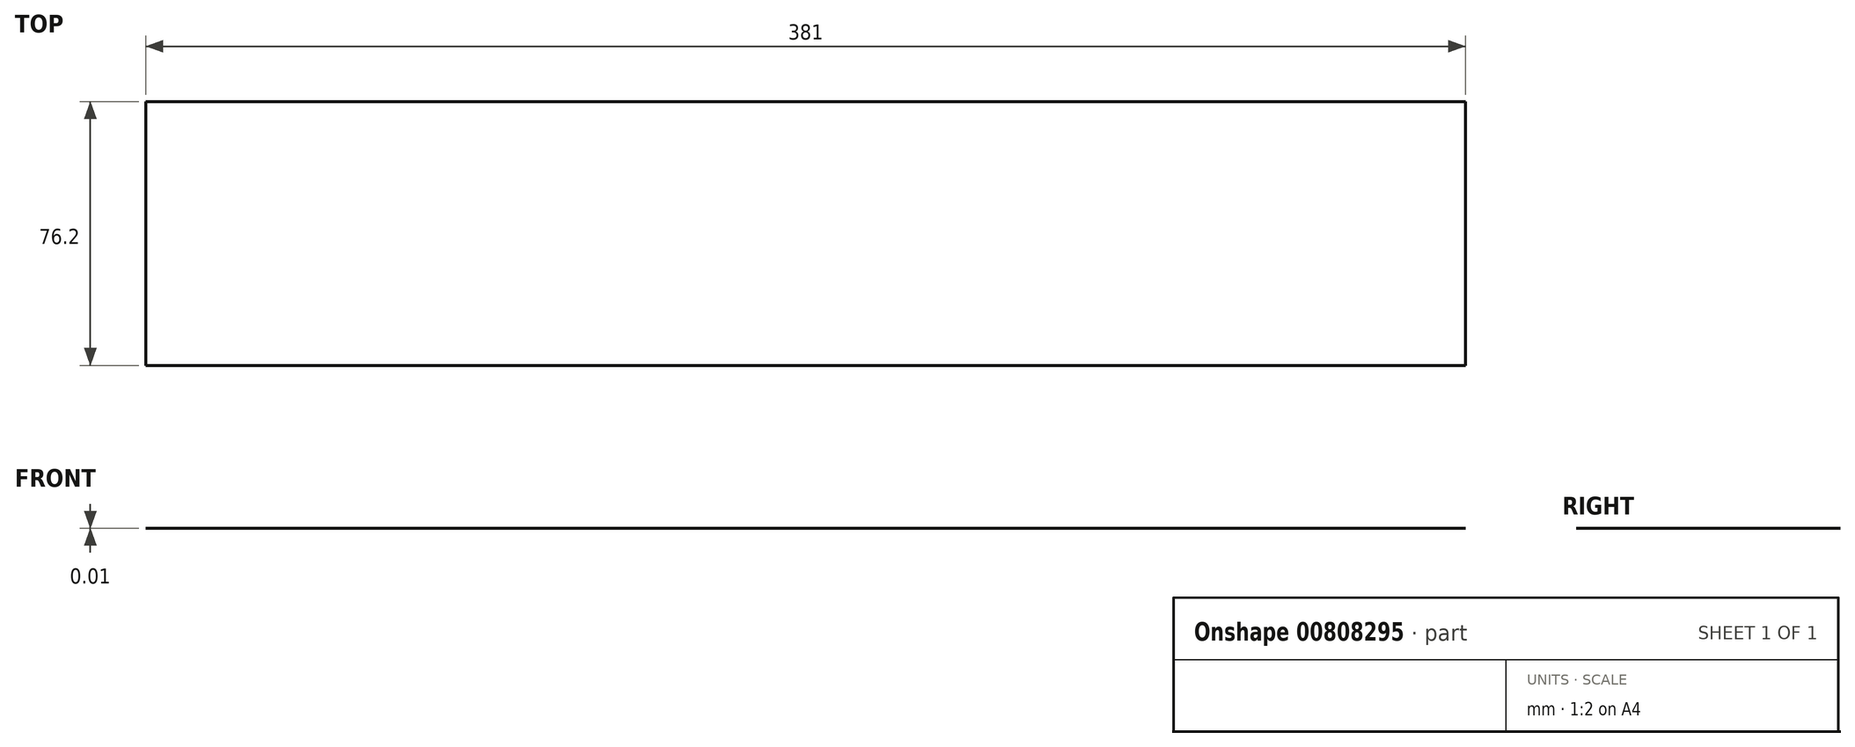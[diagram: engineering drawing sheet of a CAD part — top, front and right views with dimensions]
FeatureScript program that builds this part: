
annotation { "Feature Type Name" : "Feature", "Feature Type Description" : "" }
export const myFeature = defineFeature(function(context is Context, id is Id, definition is map)
    precondition{}
    {
        {
            var Q0;
            Q0=qCreatedBy(makeId("Top.planeOp"),FACE);
            var sketch = newSketch(context, id + "F0", { "sketchPlane" : qUnion([Q0])});
            skLineSegment(sketch, "E0.bottom", {"start": v(190.5, -38.1) * mm, "end": v(-190.5, -38.1) * mm});
            skLineSegment(sketch, "E0.top", {"start": v(190.5, 38.1) * mm, "end": v(-190.5, 38.1) * mm});
            skLineSegment(sketch, "E0.left", {"start": v(190.5, -38.1) * mm, "end": v(190.5, 38.1) * mm});
            skLineSegment(sketch, "E0.right", {"start": v(-190.5, -38.1) * mm, "end": v(-190.5, 38.1) * mm});
            skPoint(sketch, "E0.middle", {"position": v(0, 0) * mm});
            skSolve(sketch);
        }
        {
            var Q0;
            Q0=qSketchRegion(id+"F0",true);
            extrude(context, id + "F1", {"entities" : qUnion([Q0]), "depth" : 3 / 203.2 * mm, "offsetDistance" : 25 * mm});
        }
    });
